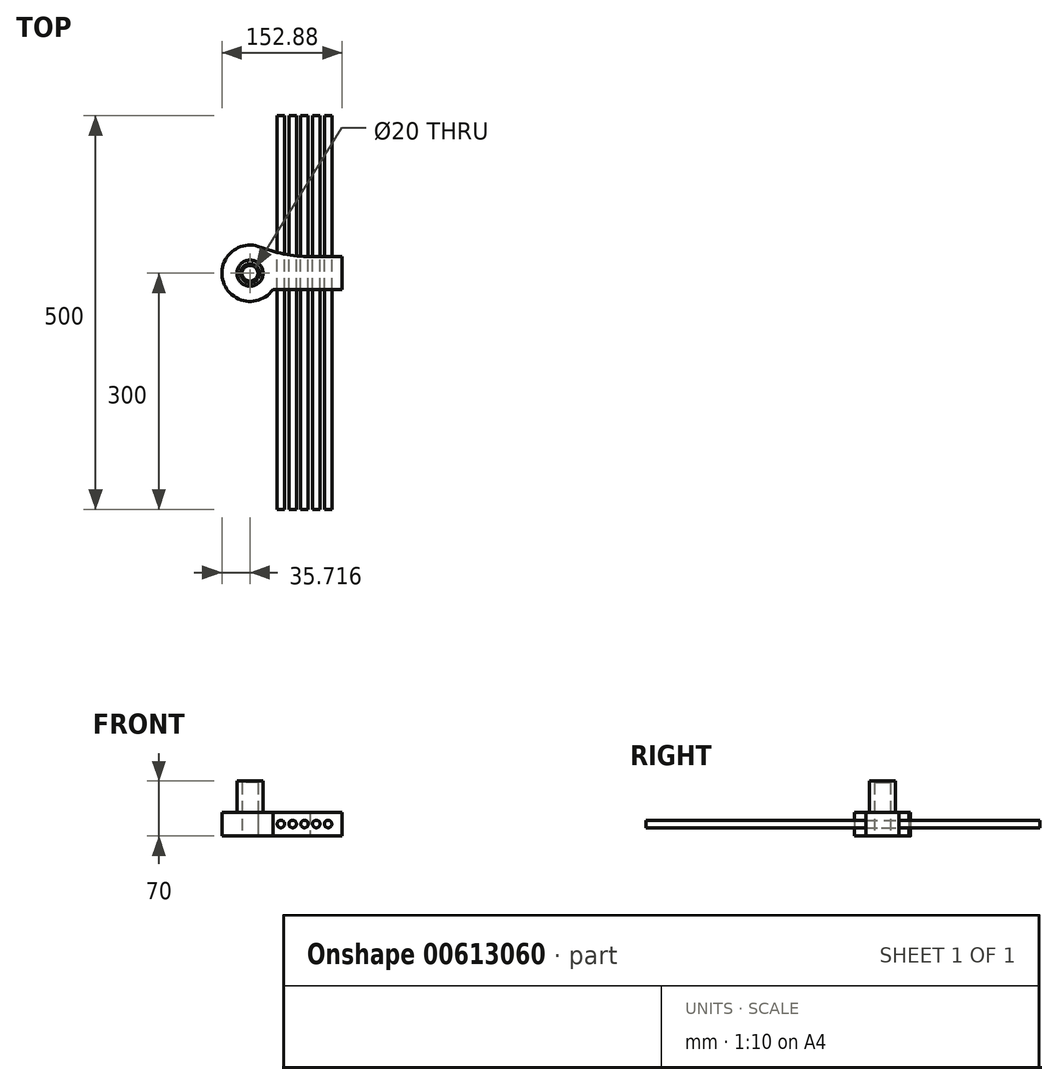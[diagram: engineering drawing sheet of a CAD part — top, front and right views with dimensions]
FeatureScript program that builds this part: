
annotation { "Feature Type Name" : "Feature", "Feature Type Description" : "" }
export const myFeature = defineFeature(function(context is Context, id is Id, definition is map)
    precondition{}
    {
        {
            var Q0;
            Q0=qCreatedBy(makeId("Top.planeOp"),FACE);
            var sketch = newSketch(context, id + "F0", { "sketchPlane" : qUnion([Q0])});
            skLineSegment(sketch, "E0.bottom", {"start": v(58.58, -20.9) * mm, "end": v(-58.58, -20.9) * mm});
            skLineSegment(sketch, "E0.top", {"start": v(58.58, 20.9) * mm, "end": v(-58.58, 20.9) * mm});
            skLineSegment(sketch, "E0.left", {"start": v(58.58, -20.9) * mm, "end": v(58.58, 20.9) * mm});
            skLineSegment(sketch, "E0.right", {"start": v(-58.58, -20.9) * mm, "end": v(-58.58, 20.9) * mm});
            skPoint(sketch, "E0.middle", {"position": v(0, 0) * mm});
            skCircle(sketch, "E1", {"center": v(-58.58, 0) * mm, "radius": 35.71 * mm});
            skCircle(sketch, "E2", {"center": v(-58.58, 0) * mm, "radius": 10 * mm});
            skArc(sketch, "E3", {"start": v(-48.05, 34.13) * mm, "mid": v(-15.72, 24.54) * mm, "end": v(17.8, 20.9) * mm});
            skCircle(sketch, "E4", {"center": v(-58.58, 0) * mm, "radius": 16.57 * mm});
            skSolve(sketch);
        }
        {
            var Q0;
            {var subQ0=sQuery(id+"F0.wireOp",EDGE,"E0.right");var subQ10=sQuery(id+"F0.wireOp",EDGE,"E0.bottom");var subQ11=makeQuery(id+"F0.imprint","INTERSECT",VERTEX,{"derivedFrom":[subQ10,subQ0]});Q0=makeQuery(id+"F0.imprint","IMPRINT",FACE,{"disambiguationData":[TD([[makeQuery(id+"F0.imprint","IMPRINT",EDGE,{"disambiguationData":[TD([[subQ11,1.0]])],"derivedFrom":subQ10}),1.0]])]});}
            var Q1;
            {var subQ0=sQuery(id+"F0.wireOp",EDGE,"E0.right");var subQ7=sQuery(id+"F0.wireOp",EDGE,"E0.bottom");var subQ8=makeQuery(id+"F0.imprint","INTERSECT",VERTEX,{"derivedFrom":[subQ7,subQ0]});Q1=makeQuery(id+"F0.imprint","IMPRINT",FACE,{"disambiguationData":[TD([[makeQuery(id+"F0.imprint","IMPRINT",EDGE,{"disambiguationData":[TD([[subQ8,1.0]])],"derivedFrom":subQ7}),-1.0]])]});}
            var Q2;
            {var subQ0=sQuery(id+"F0.wireOp",EDGE,"E3");var subQ1=sQuery(id+"F0.wireOp",EDGE,"E0.top");var subQ2=makeQuery(id+"F0.imprint","INTERSECT",VERTEX,{"derivedFrom":[subQ1,subQ0]});Q2=makeQuery(id+"F0.imprint","IMPRINT",FACE,{"disambiguationData":[TD([[makeQuery(id+"F0.imprint","IMPRINT",EDGE,{"disambiguationData":[TD([[subQ2,-1.0]])],"derivedFrom":subQ1}),-1.0]])]});}
            var Q3;
            {var subQ4=sQuery(id+"F0.wireOp",EDGE,"E0.left");Q3=makeQuery(id+"F0.imprint","IMPRINT",FACE,{"disambiguationData":[TD([[makeQuery(id+"F0.imprint","IMPRINT",EDGE,{"derivedFrom":subQ4}),1.0]])]});}
            extrude(context, id + "F1", {"entities" : qUnion([Q0, Q1, Q2, Q3]), "depth" : 30 * mm, "offsetDistance" : 25 * mm});
        }
        {
            var Q0;
            {var subQ0=sQuery(id+"F0.wireOp",EDGE,"E4");var subQ1=sQuery(id+"F0.wireOp",EDGE,"E0.right");var subQ2=makeQuery(id+"F0.imprint","INTERSECT",VERTEX,{"disambiguationData":[OD(0.0)],"derivedFrom":[subQ1,subQ0]});Q0=makeQuery(id+"F0.imprint","IMPRINT",FACE,{"disambiguationData":[TD([[makeQuery(id+"F0.imprint","IMPRINT",EDGE,{"disambiguationData":[TD([[subQ2,-1.0]])],"derivedFrom":subQ1}),1.0]])]});}
            var Q1;
            {var subQ0=sQuery(id+"F0.wireOp",EDGE,"E4");var subQ1=sQuery(id+"F0.wireOp",EDGE,"E0.right");var subQ2=makeQuery(id+"F0.imprint","INTERSECT",VERTEX,{"disambiguationData":[OD(0.0)],"derivedFrom":[subQ1,subQ0]});Q1=makeQuery(id+"F0.imprint","IMPRINT",FACE,{"disambiguationData":[TD([[makeQuery(id+"F0.imprint","IMPRINT",EDGE,{"disambiguationData":[TD([[subQ2,-1.0]])],"derivedFrom":subQ1}),-1.0]])]});}
            var Q2;
            Q2=sQuery(id+"F0.wireOp",EDGE,"E2");
            var Q3;
            Q3=sQuery(id+"F0.wireOp",EDGE,"E4");
            var Q4;
            Q4=sQuery(id+"F0.wireOp",EDGE,"E3");
            var Q5;
            Q5=sQuery(id+"F0.wireOp",EDGE,"E0.bottom");
            var Q6;
            Q6=sQuery(id+"F0.wireOp",EDGE,"E0.left");
            var Q7;
            Q7=sQuery(id+"F0.wireOp",EDGE,"E0.right");
            extrude(context, id + "F2", {"entities" : qUnion([Q0, Q1]), "operationType" : NewBodyOperationType.ADD, "surfaceEntities" : qUnion([Q2, Q3, Q4, Q5, Q6, Q7]), "depth" : 70 * mm, "offsetDistance" : 25 * mm});
        }
        {
            var Q0;
            Q0=makeQuery(id+"F2.opExtrude","CAP_EDGE",EDGE,{"disambiguationData":[OSD([sQuery(id+"F0.wireOp",EDGE,"E2")])],"isStart":false});
            chamfer(context, id + "F3", {"entities" : qUnion([Q0]), "width" : 2 * mm, "tangentPropagation" : true});
        }
        {
            var Q0;
            Q0=qCreatedBy(makeId("Front.planeOp"),FACE);
            var sketch = newSketch(context, id + "F4", { "sketchPlane" : qUnion([Q0])});
            skCircle(sketch, "E5", {"center": v(-19.36, 15.3) * mm, "radius": 4.76 * mm});
            skCircle(sketch, "E6.1.0.0", {"center": v(-4.36, 15.3) * mm, "radius": 4.76 * mm});
            skCircle(sketch, "E6.2.0.0", {"center": v(10.64, 15.3) * mm, "radius": 4.76 * mm});
            skCircle(sketch, "E6.3.0.0", {"center": v(25.64, 15.3) * mm, "radius": 4.76 * mm});
            skCircle(sketch, "E6.4.0.0", {"center": v(40.64, 15.3) * mm, "radius": 4.76 * mm});
            skLineSegment(sketch, "E6.direction1", {"start": v(-19.36, 15.3) * mm, "end": v(-4.36, 15.3) * mm, "construction": true});
            skSolve(sketch);
        }
        {
            var Q0;
            Q0 = qSketchRegion(id + "F4", true);
            extrude(context, id + "F5", {"entities" : qUnion([Q0]), "depth" : 300 * mm, "offsetDistance" : 25 * mm, "hasSecondDirection" : true, "secondDirectionOppositeDirection" : true, "secondDirectionDepth" : 200 * mm});
        }
    });
